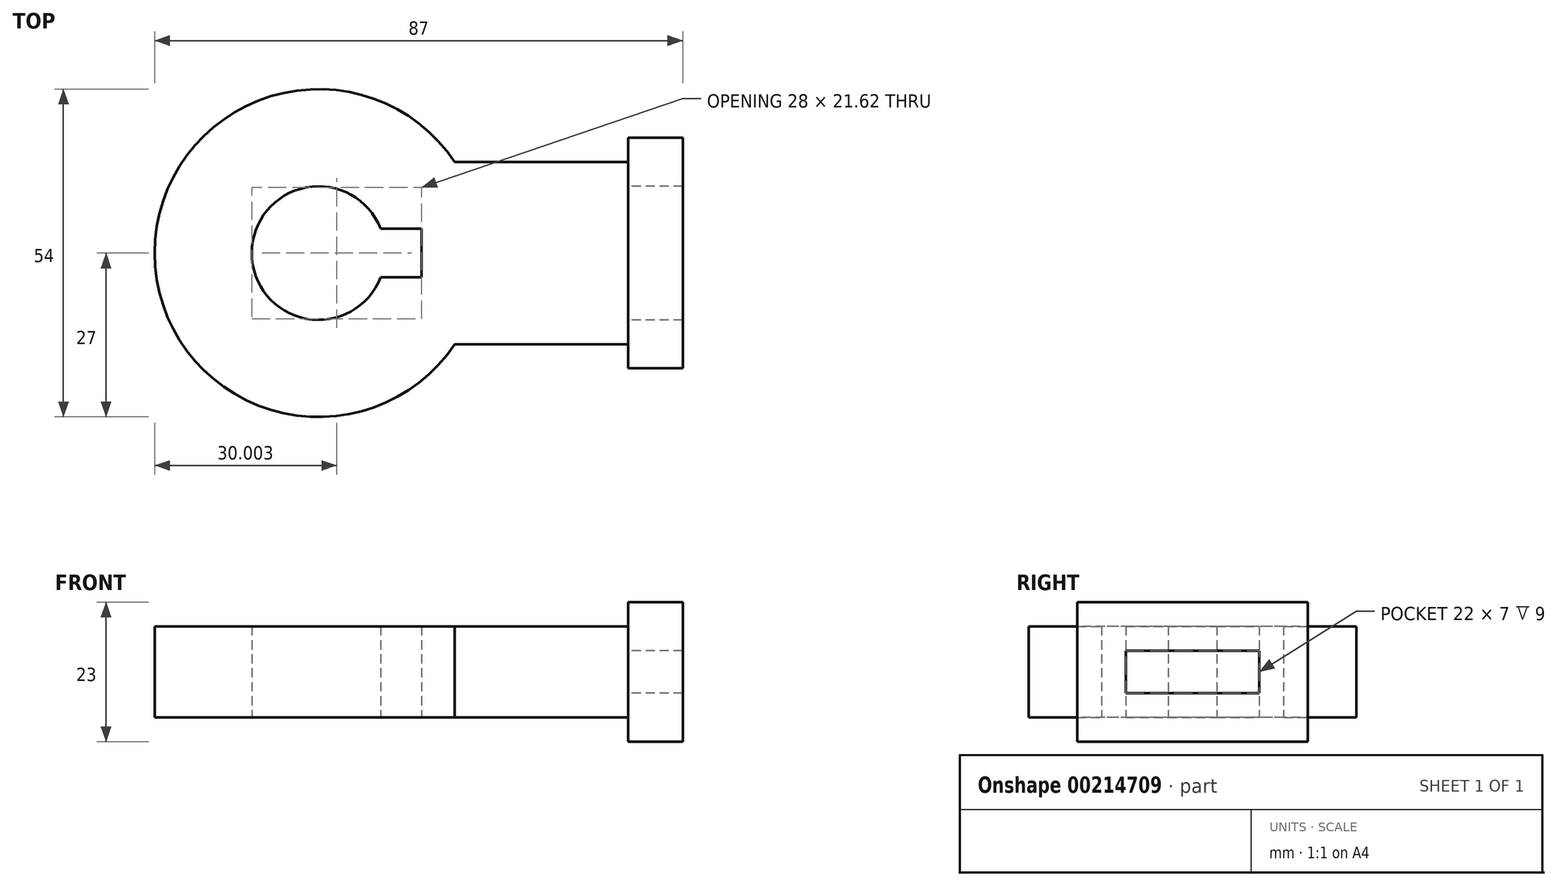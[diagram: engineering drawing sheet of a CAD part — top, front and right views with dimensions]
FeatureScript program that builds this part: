
annotation { "Feature Type Name" : "Feature", "Feature Type Description" : "" }
export const myFeature = defineFeature(function(context is Context, id is Id, definition is map)
    precondition{}
    {
        {
            var Q0;
            Q0=qCreatedBy(makeId("Top.planeOp"),FACE);
            var sketch = newSketch(context, id + "F0", { "sketchPlane" : qUnion([Q0])});
            skLineSegment(sketch, "E0", {"start": v(4.83, -20.55) * mm, "end": v(4.83, -35.55) * mm});
            skLineSegment(sketch, "E1", {"start": v(4.83, -20.55) * mm, "end": v(4.83, -5.55) * mm});
            skLineSegment(sketch, "E2", {"start": v(4.83, -5.55) * mm, "end": v(-23.72, -5.55) * mm});
            skLineSegment(sketch, "E3", {"start": v(4.83, -35.55) * mm, "end": v(-23.72, -35.55) * mm});
            skArc(sketch, "E4", {"start": v(-23.72, -35.55) * mm, "mid": v(-73.17, -20.55) * mm, "end": v(-23.72, -5.55) * mm});
            skLineSegment(sketch, "E5", {"start": v(-29.17, -20.55) * mm, "end": v(-29.17, -16.55) * mm});
            skLineSegment(sketch, "E6", {"start": v(-29.17, -16.55) * mm, "end": v(-35.92, -16.55) * mm});
            skLineSegment(sketch, "E7", {"start": v(-29.17, -20.55) * mm, "end": v(-29.17, -24.55) * mm});
            skLineSegment(sketch, "E8", {"start": v(-29.17, -24.55) * mm, "end": v(-35.92, -24.55) * mm});
            skArc(sketch, "E9", {"start": v(-35.92, -24.55) * mm, "mid": v(-57.17, -20.55) * mm, "end": v(-35.92, -16.55) * mm});
            skSolve(sketch);
        }
        {
            var Q0;
            Q0=makeQuery(id+"F0.imprint","IMPRINT",FACE,{"disambiguationData":[TD([[makeQuery(id+"F0.imprint","IMPRINT",EDGE,{"derivedFrom":sQuery(id+"F0.wireOp",EDGE,"E0")}),-1.0]])]});
            extrude(context, id + "F1", {"entities" : qUnion([Q0]), "depth" : 15 * mm});
        }
        {
            var Q0;
            Q0=makeQuery(id+"F1.opExtrude","SWEPT_FACE",FACE,{"disambiguationData":[OSD([sQuery(id+"F0.wireOp",EDGE,"E0"),sQuery(id+"F0.wireOp",EDGE,"E1")])]});
            var sketch = newSketch(context, id + "F2", { "sketchPlane" : qUnion([Q0])});
            skPoint(sketch, "E10.endSnap0", {"position": v(-35.55, 7.5) * mm});
            skPoint(sketch, "E10.endSnap1", {"position": v(-20.55, 15) * mm});
            skLineSegment(sketch, "E11", {"start": v(-20.55, 11) * mm, "end": v(-9.55, 11) * mm});
            skLineSegment(sketch, "E12", {"start": v(-9.55, 11) * mm, "end": v(-9.55, 4) * mm});
            skLineSegment(sketch, "E13", {"start": v(-9.55, 4) * mm, "end": v(-20.55, 4) * mm});
            skLineSegment(sketch, "E14", {"start": v(-20.55, 4) * mm, "end": v(-31.55, 4) * mm});
            skLineSegment(sketch, "E15", {"start": v(-31.55, 4) * mm, "end": v(-31.55, 11) * mm});
            skLineSegment(sketch, "E16", {"start": v(-31.55, 11) * mm, "end": v(-20.55, 11) * mm});
            skLineSegment(sketch, "E17", {"start": v(-20.55, 19) * mm, "end": v(-1.55, 19) * mm});
            skLineSegment(sketch, "E18", {"start": v(-1.55, 19) * mm, "end": v(-1.55, -4) * mm});
            skLineSegment(sketch, "E19", {"start": v(-1.55, -4) * mm, "end": v(-39.55, -4) * mm});
            skLineSegment(sketch, "E20", {"start": v(-39.55, -4) * mm, "end": v(-39.55, 19) * mm});
            skLineSegment(sketch, "E21", {"start": v(-39.55, 19) * mm, "end": v(-20.55, 19) * mm});
            skSolve(sketch);
        }
        {
            var Q0;
            Q0 = qSketchRegion(id + "F2", true);
            extrude(context, id + "F3", {"entities" : qUnion([Q0]), "operationType" : NewBodyOperationType.ADD, "depth" : 9 * mm});
        }
    });
